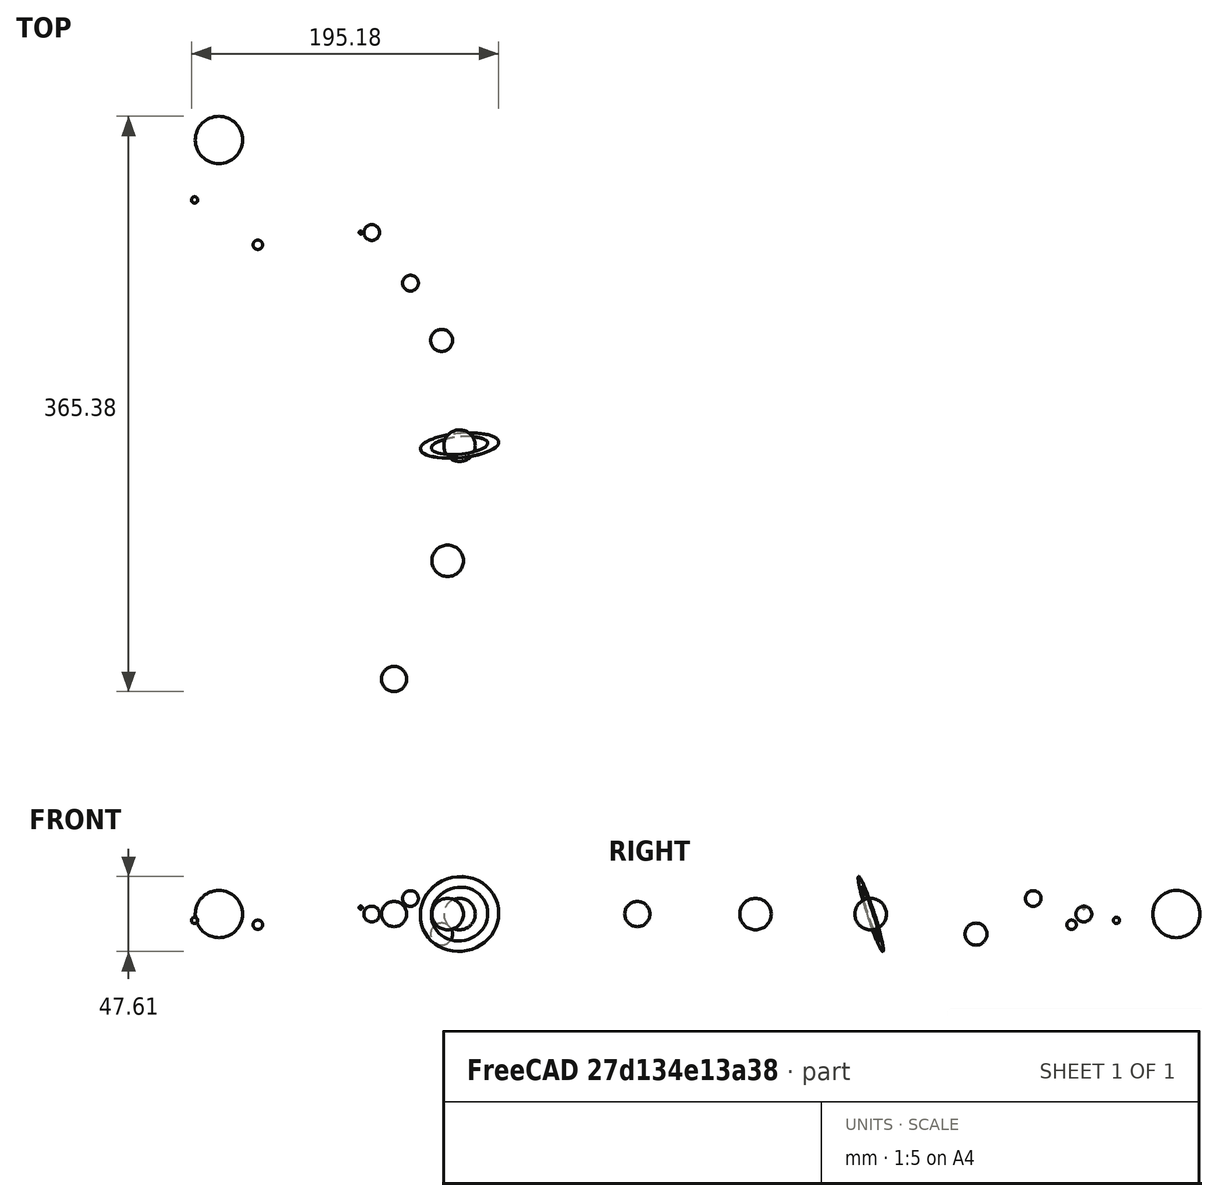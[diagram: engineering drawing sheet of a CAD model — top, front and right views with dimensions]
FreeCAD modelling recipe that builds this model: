
FCSTD DOCUMENT  (FreeCAD 0.18R14555 (Git shallow))
Label: SOLAR SYSTEM
License: All rights reserved
LicenseURL: http://en.wikipedia.org/wiki/All_rights_reserved
objects: App::DocumentObjectGroupPython×12, Part::Sphere×10, Part::Ellipse×7, Part::Compound×2, Part::Cylinder×2, Part::Cut×1, Part::Circle×1
note: 23 computed .brp shape members not serialized (recipe doc carries the construction recipe); baked Part::Feature solids carry a one-line shape summary decoded from their .brp

FEATURE [Part::Ellipse] Ellipse
  Angle0 = 0
  Angle1 = 360
  AttacherType = Attacher::AttachEngine3D
  MajorRadius = 50
  MinorRadius = 40
  Placement = pos=(0,0,0) rot=(0,-1,0;0.261799rad)
FEATURE [Part::Sphere] Sphere  label="Mercury"
  Angle1 = -90
  Angle2 = 90
  Angle3 = 360
  AttacherType = Attacher::AttachEngine3D
  Placement = pos=(-15.4508,-38.0423,-4.01722) rot=(0,0,1;4.39823rad)
  Radius = 2
FEATURE [App::DocumentObjectGroupPython] My_Placer  label="Mercury001"  # scripted group (container) (typed FeaturePython)
  Placement = pos=(-15.4508,-38.0423,-4.01722) rot=(0,0,1;16.9646rad)
  RotAxis = (0,0,1)
  RotCenter = (0,0,0)
  arc = time*1080
  arc0 = 0
  arc1 = 90
  target = -> Sphere
  time = 0.9
  x = 50*x0
  x0 = -0.309017
  x1 = 200
  y = 40*y0
  y0 = -0.951057
  y1 = 0
  z = 13*x0
  z0 = 0
  z1 = 0
  expr: y0 = sin(time * 1080)
  expr: x0 = cos(time * 1080)
FEATURE [Part::Ellipse] Ellipse001
  Angle0 = 0
  Angle1 = 360
  AttacherType = Attacher::AttachEngine3D
  MajorRadius = 80
  MinorRadius = 70
  Placement = pos=(0,0,0) rot=(0,1,0;0.261799rad)
FEATURE [Part::Sphere] Sphere001  label="Venus"
  Angle1 = -90
  Angle2 = 90
  Angle3 = 360
  AttacherType = Attacher::AttachEngine3D
  Placement = pos=(24.7214,-66.574,-6.79837) rot=(0,0,1;5.02655rad)
  Radius = 3
FEATURE [App::DocumentObjectGroupPython] My_Placer001  label="Venus001"  # scripted group (container) (typed FeaturePython)
  Placement = pos=(24.7214,-66.574,-6.79837) rot=(0,0,1;11.3097rad)
  RotAxis = (0,0,1)
  RotCenter = (0,0,0)
  arc = time*720
  arc0 = 0
  arc1 = 90
  target = -> Sphere001
  time = 0.9
  x = 80*x0
  x0 = 0.309017
  x1 = 200
  y = 70*y0
  y0 = -0.951057
  y1 = 0
  z = -22*x0
  z0 = 0
  z1 = 0
  expr: y0 = sin(time * 720)
  expr: x0 = cos(time * 720)
FEATURE [Part::Sphere] Sphere002  label="Earth"
  Angle1 = -90
  Angle2 = 90
  Angle3 = 360
  AttacherType = Attacher::AttachEngine3D
  Placement = pos=(0,0,0) rot=(0,0,1;5.65487rad)
  Radius = 5
FEATURE [Part::Sphere] Sphere003  label="Moon"
  Angle1 = -90
  Angle2 = 90
  Angle3 = 360
  AttacherType = Attacher::AttachEngine3D
  Placement = pos=(-5.66312,-4.1145,4.1145) rot=(0,0,1;3.76991rad)
  Radius = 1
FEATURE [App::DocumentObjectGroupPython] My_Placer002  label="Earth001"  # scripted group (container) (typed FeaturePython)
  Placement = pos=(0,0,0) rot=(0,0,1;5.65487rad)
  RotAxis = (0,0,1)
  RotCenter = (0,0,0)
  arc = time*360
  arc0 = 0
  arc1 = 90
  target = -> Sphere002
  time = 0.9
  x = 0
  x0 = 0
  x1 = 200
  y = 0
  y0 = 0
  y1 = 0
  z = 0
  z0 = 0
  z1 = 0
FEATURE [App::DocumentObjectGroupPython] My_Placer003  label="Moon001"  # scripted group (container) (typed FeaturePython)
  Placement = pos=(-5.66312,-4.1145,4.1145) rot=(0,0,1;22.6195rad)
  RotAxis = (0,0,1)
  RotCenter = (0,0,0)
  arc = time*1440
  arc0 = 0
  arc1 = 90
  target = -> Sphere003
  time = 0.9
  x = x0*7
  x0 = -0.809017
  x1 = 200
  y = y0*7
  y0 = -0.587785
  y1 = 0
  z = -y0*7
  z0 = 0
  z1 = 0
  expr: y0 = sin(time * 1440)
  expr: x0 = cos(time * 1440)
FEATURE [Part::Compound] Compound
  Links = -> [Sphere002,Sphere003]
  Placement = pos=(97.082,-58.7785,0) rot=(0,0,1;5.65487rad)
FEATURE [App::DocumentObjectGroupPython] My_Placer004  label="Earth+Moon"  # scripted group (container) (typed FeaturePython)
  Placement = pos=(97.082,-58.7785,0) rot=(0,0,1;5.65487rad)
  RotAxis = (0,0,1)
  RotCenter = (0,0,0)
  arc = time*360
  arc0 = 0
  arc1 = 90
  target = -> Compound
  time = 0.9
  x = 120*x0
  x0 = 0.809017
  x1 = 200
  y = 100*y0
  y0 = -0.587785
  y1 = 0
  z = 0
  z0 = 0
  z1 = 0
  expr: y0 = sin(time * 360)
  expr: x0 = cos(time * 360)
FEATURE [Part::Ellipse] Ellipse003
  Angle0 = 0
  Angle1 = 360
  AttacherType = Attacher::AttachEngine3D
  MajorRadius = 160
  MinorRadius = 140
  Placement = pos=(0,0,0) rot=(0,-1,0;0.087266rad)
FEATURE [Part::Sphere] Sphere004  label="Mars"
  Angle1 = -90
  Angle2 = 90
  Angle3 = 360
  AttacherType = Attacher::AttachEngine3D
  Placement = pos=(121.665,-90.9227,9.88528) rot=(0,0,1;5.65487rad)
  Radius = 5
FEATURE [App::DocumentObjectGroupPython] My_Placer005  label="Mars001"  # scripted group (container) (typed FeaturePython)
  Placement = pos=(121.665,-90.9227,9.88528) rot=(0,0,1;5.65487rad)
  RotAxis = (0,0,1)
  RotCenter = (0,0,0)
  arc = time*360
  arc0 = 0
  arc1 = 90
  target = -> Sphere004
  time = 0.9
  x = 160*x0
  x0 = 0.760406
  x1 = 200
  y = 140*y0
  y0 = -0.649448
  y1 = 0
  z = 13*x0
  z0 = 0
  z1 = 0
  expr: y0 = sin(time * 355)
  expr: x0 = cos(time * 355)
FEATURE [Part::Ellipse] Ellipse004
  Angle0 = 0
  Angle1 = 360
  AttacherType = Attacher::AttachEngine3D
  MajorRadius = 200
  MinorRadius = 180
  Placement = pos=(0,0,0) rot=(0,1,0;0.087266rad)
FEATURE [Part::Sphere] Sphere005  label="Jupiter"
  Angle1 = -90
  Angle2 = 90
  Angle3 = 360
  AttacherType = Attacher::AttachEngine3D
  Placement = pos=(141.421,-127.279,-12.7279) rot=(0,0,1;5.65487rad)
  Radius = 7
FEATURE [App::DocumentObjectGroupPython] My_Placer006  label="Jupiter001"  # scripted group (container) (typed FeaturePython)
  Placement = pos=(141.421,-127.279,-12.7279) rot=(0,0,1;5.65487rad)
  RotAxis = (0,0,1)
  RotCenter = (0,0,0)
  arc = time*360
  arc0 = 0
  arc1 = 90
  target = -> Sphere005
  time = 0.9
  x = 200*x0
  x0 = 0.707107
  x1 = 200
  y = 180*y0
  y0 = -0.707107
  y1 = 0
  z = -18*x0
  z0 = 0
  z1 = 0
  expr: y0 = sin(time * 350)
  expr: x0 = cos(time * 350)
FEATURE [Part::Ellipse] Ellipse005
  Angle0 = 0
  Angle1 = 360
  AttacherType = Attacher::AttachEngine3D
  MajorRadius = 260
  MinorRadius = 240
FEATURE [Part::Sphere] Sphere006  label="Saturn"
  Angle1 = -90
  Angle2 = 90
  Angle3 = 360
  AttacherType = Attacher::AttachEngine3D
  Radius = 10
FEATURE [Part::Cylinder] Cylinder
  Angle = 360
  AttacherType = Attacher::AttachEngine3D
  Height = 0.1
  Radius = 25
FEATURE [Part::Cylinder] Cylinder001
  Angle = 360
  AttacherType = Attacher::AttachEngine3D
  Height = 10
  Radius = 18
FEATURE [Part::Cut] Cut
  Base = -> Cylinder
  Placement = pos=(0,0,0) rot=(0,-1,0;0.087266rad)
  Tool = -> Cylinder001
FEATURE [Part::Compound] Compound001  label="Saturn001"
  Links = -> [Sphere006,Cut]
  Placement = pos=(152.824,-194.164,0) rot=(1,0,0;5.02655rad)
FEATURE [App::DocumentObjectGroupPython] My_Placer007  label="Saturn002"  # scripted group (container) (typed FeaturePython)
  Placement = pos=(152.824,-194.164,0) rot=(1,0,0;11.3097rad)
  RotAxis = (1,0,0)
  RotCenter = (0,0,0)
  arc = time*720
  arc0 = 0
  arc1 = 90
  target = -> Compound001
  time = 0.9
  x = 260*x0
  x0 = 0.587785
  x1 = 200
  y = 240*y0
  y0 = -0.809017
  y1 = 0
  z = 0
  z0 = 0
  z1 = 0
  expr: y0 = sin(time * 340)
  expr: x0 = cos(time * 340)
FEATURE [Part::Ellipse] Ellipse006
  Angle0 = 0
  Angle1 = 360
  AttacherType = Attacher::AttachEngine3D
  MajorRadius = 120
  MinorRadius = 100
FEATURE [Part::Ellipse] Ellipse007
  Angle0 = 0
  Angle1 = 360
  AttacherType = Attacher::AttachEngine3D
  MajorRadius = 320
  MinorRadius = 300
FEATURE [Part::Sphere] Sphere007  label="Uranus"
  Angle1 = -90
  Angle2 = 90
  Angle3 = 360
  AttacherType = Attacher::AttachEngine3D
  Placement = pos=(145.277,-267.302,0) rot=(0,0,1;5.65487rad)
  Radius = 10
FEATURE [App::DocumentObjectGroupPython] My_Placer008  label="Uranus001"  # scripted group (container) (typed FeaturePython)
  Placement = pos=(145.277,-267.302,0) rot=(0,0,1;5.65487rad)
  RotAxis = (0,0,1)
  RotCenter = (0,0,0)
  arc = time*360
  arc0 = 0
  arc1 = 90
  target = -> Sphere007
  time = 0.9
  x = 320*x0
  x0 = 0.45399
  x1 = 200
  y = 300*y0
  y0 = -0.891007
  y1 = 0
  z = 0
  z0 = 0
  z1 = 0
  expr: y0 = sin(time * 330)
  expr: x0 = cos(time * 330)
FEATURE [Part::Circle] Circle
  Angle0 = 0
  Angle1 = 360
  AttacherType = Attacher::AttachEngine3D
  Radius = 360
FEATURE [Part::Sphere] Sphere008  label="Neptuno"
  Angle1 = -90
  Angle2 = 90
  Angle3 = 360
  AttacherType = Attacher::AttachEngine3D
  Placement = pos=(111.246,-342.38,0) rot=(0,0,1;5.65487rad)
  Radius = 8
FEATURE [App::DocumentObjectGroupPython] My_Placer009  label="Neptuno001"  # scripted group (container) (typed FeaturePython)
  Placement = pos=(111.246,-342.38,0) rot=(0,0,1;5.65487rad)
  RotAxis = (0,0,1)
  RotCenter = (0,0,0)
  arc = time*360
  arc0 = 0
  arc1 = 90
  target = -> Sphere008
  time = 0.9
  x = 360*x0
  x0 = 0.309017
  x1 = 200
  y = 360*y0
  y0 = -0.951057
  y1 = 0
  z = 0
  z0 = 0
  z1 = 0
  expr: y0 = sin(time * 320)
  expr: x0 = cos(time * 320)
FEATURE [Part::Sphere] Sphere009  label="SUN"
  Angle1 = -90
  Angle2 = 90
  Angle3 = 360
  AttacherType = Attacher::AttachEngine3D
  Placement = pos=(0,0,0) rot=(0,0,1;0.628319rad)
  Radius = 15
FEATURE [App::DocumentObjectGroupPython] My_Placer010  label="SUN001"  # scripted group (container) (typed FeaturePython)
  Placement = pos=(0,0,0) rot=(0,0,1;-37.0708rad)
  RotAxis = (0,0,1)
  RotCenter = (0,0,0)
  arc = -time*2360
  arc0 = 0
  arc1 = 90
  target = -> Sphere009
  time = 0.9
  x = 0
  x0 = 0
  x1 = 200
  y = 0
  y0 = 0
  y1 = 0
  z = 0
  z0 = 0
  z1 = 0
FEATURE [App::DocumentObjectGroupPython] My_Manager  # scripted group (container) (typed FeaturePython)
  Group = -> [My_Placer,My_Placer001,My_Placer002,My_Placer003,My_Placer004,My_Placer005,My_Placer006,My_Placer007,My_Placer008,My_Placer009,My_Placer010]
  intervall = 1000
  sleeptime = 0.02
  start = 0
  step = 91
  text = NO
